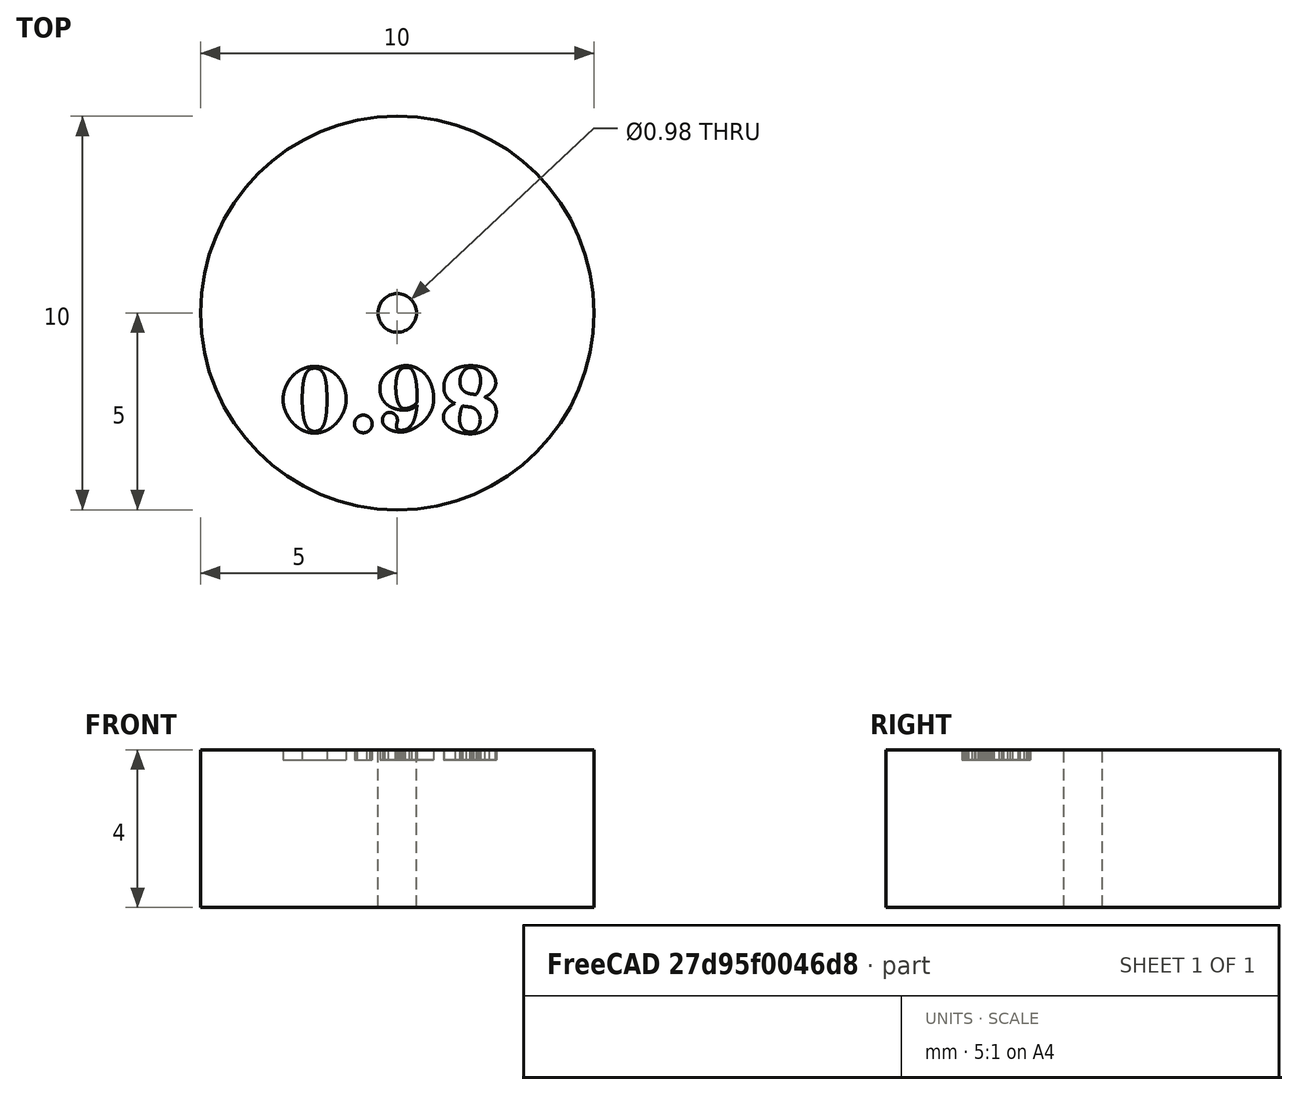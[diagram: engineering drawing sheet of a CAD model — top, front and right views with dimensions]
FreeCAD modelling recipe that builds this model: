
FCSTD DOCUMENT  (FreeCAD 0.19R24276 (Git))
Label: HoleTest
License: All rights reserved
LicenseURL: http://en.wikipedia.org/wiki/All_rights_reserved
objects: Part::Part2DObjectPython×2, Part::FeaturePython×1, Part::Extrusion×1, Part::Cut×1
note: 5 computed .brp shape members not serialized (recipe doc carries the construction recipe); baked Part::Feature solids carry a one-line shape summary decoded from their .brp

FEATURE [Part::FeaturePython] Tube  # WARN: FeaturePython — macro-defined, semantics opaque (R4)
  AttacherType = Attacher::AttachEngine3D
  Height = 4
  InnerRadius = 0.49
  OuterRadius = 5
FEATURE [Part::Part2DObjectPython] ShapeString001  # Draft 2D object (typed FeaturePython)
  FontFile = <userpath>/Documents/git/KiCad/Inkscape/fonts/PurplePurse-Regular.ttf
  Placement = pos=(-3,-3,4) rot=(0,0,1;0rad)
  Size = 2
  String = 0.98
  Tracking = 0
FEATURE [Part::Extrusion] Extrude
  Base = -> ShapeString001
  Dir = (0,0,1)
  DirMode = 2
  FaceMakerClass = Part::FaceMakerBullseye
  LengthFwd = -0.25
  LengthRev = 0
  Solid = false
  Symmetric = false
FEATURE [Part::Cut] Cut  label="Cut1.0"
  Base = -> Tube
  Tool = -> Extrude
FEATURE [Part::Part2DObjectPython] ShapeString002  # Draft 2D object (typed FeaturePython)
  FontFile = <userpath>/Documents/git/KiCad/Inkscape/fonts/PurplePurse-Regular.ttf
  Placement = pos=(-1,-3,4) rot=(0,0,1;0rad)
  Size = 2
  String = 0.94
  Tracking = 0
